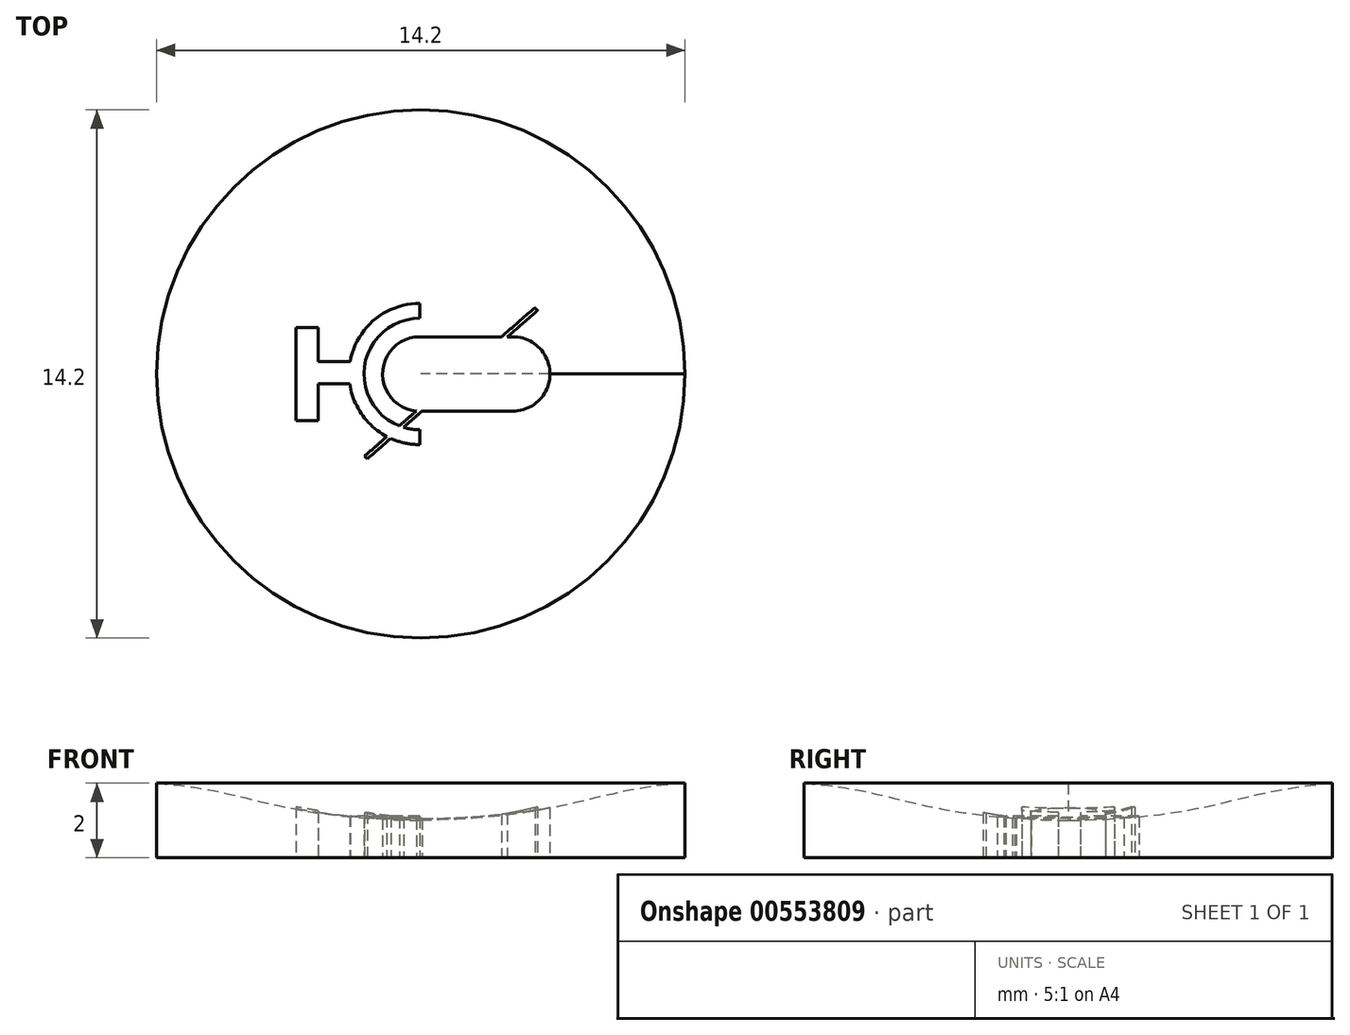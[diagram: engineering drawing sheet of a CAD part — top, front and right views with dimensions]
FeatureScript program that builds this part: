
annotation { "Feature Type Name" : "Feature", "Feature Type Description" : "" }
export const myFeature = defineFeature(function(context is Context, id is Id, definition is map)
    precondition{}
    {
        {
            var Q0;
            Q0=qCreatedBy(makeId("Front.planeOp"),FACE);
            var sketch = newSketch(context, id + "F0", { "sketchPlane" : qUnion([Q0])});
            skLineSegment(sketch, "E0", {"start": v(0, 0) * mm, "end": v(7.1, 0) * mm});
            skLineSegment(sketch, "E1", {"start": v(7.1, 0) * mm, "end": v(7.1, 2) * mm});
            skLineSegment(sketch, "E2", {"start": v(0, 1) * mm, "end": v(0, 0) * mm});
            skFitSpline(sketch, "E3", {"points": [v(7.1, 2) * mm, v(0, 1) * mm], "startDerivative": vector(-7.89, -0.57) * mm, "endDerivative": vector(-12, -0.18) * mm});
            skPoint(sketch, "E4.orphan", {"position": v(0, 2) * mm});
            skSolve(sketch);
        }
        {
            var Q0;
            Q0=makeQuery(id+"F0.imprint","IMPRINT",FACE,{"disambiguationData":[TD([[makeQuery(id+"F0.imprint","IMPRINT",EDGE,{"derivedFrom":sQuery(id+"F0.wireOp",EDGE,"E0")}),1.0]])]});
            var Q1;
            Q1=sQuery(id+"F0.wireOp",EDGE,"E2");
            revolve(context, id + "F1", {"entities" : qUnion([Q0]), "axis" : qUnion([Q1]), "revolveType" : RevolveType.FULL});
        }
        {
            var Q0;
            Q0=makeQuery(id+"F1.opRevolve","SWEPT_FACE",FACE,{"disambiguationData":[OSD([sQuery(id+"F0.wireOp",EDGE,"E0")])]});
            var sketch = newSketch(context, id + "F2", { "sketchPlane" : qUnion([Q0])});
            skLineSegment(sketch, "E5.bottom", {"start": v(2.47, 1) * mm, "end": v(0.04, 1) * mm});
            skLineSegment(sketch, "E5.top", {"start": v(2.47, -1) * mm, "end": v(2.33, -1) * mm});
            skArc(sketch, "E6", {"start": v(-0.12, 1) * mm, "mid": v(-1.03, -0.05) * mm, "end": v(-0.03, -1) * mm});
            skArc(sketch, "E7", {"start": v(2.47, -1) * mm, "mid": v(3.47, 0) * mm, "end": v(2.47, 1) * mm});
            skArc(sketch, "E8", {"start": v(-0.03, 1.5) * mm, "mid": v(-0.25, 1.48) * mm, "end": v(-0.46, 1.44) * mm});
            skArc(sketch, "E9.0", {"start": v(-0.03, 1.9) * mm, "mid": v(-0.42, 1.86) * mm, "end": v(-0.8, 1.73) * mm});
            skLineSegment(sketch, "E10", {"start": v(-0.03, -1.9) * mm, "end": v(-0.03, -1.5) * mm});
            skLineSegment(sketch, "E11.trimOffspring", {"start": v(-0.03, 1.5) * mm, "end": v(-0.03, 1.9) * mm});
            skLineSegment(sketch, "E12.bottom", {"start": v(-1.9, 0.27) * mm, "end": v(-2.75, 0.27) * mm});
            skLineSegment(sketch, "E12.top", {"start": v(-1.9, -0.33) * mm, "end": v(-2.75, -0.33) * mm});
            skLineSegment(sketch, "E13.bottom", {"start": v(-3.35, 1.25) * mm, "end": v(-2.75, 1.25) * mm});
            skLineSegment(sketch, "E13.top", {"start": v(-3.35, -1.25) * mm, "end": v(-2.75, -1.25) * mm});
            skLineSegment(sketch, "E13.left", {"start": v(-3.35, 1.25) * mm, "end": v(-3.35, -1.25) * mm});
            skLineSegment(sketch, "E13.right", {"start": v(-2.75, 1.25) * mm, "end": v(-2.75, 0.27) * mm});
            skLineSegment(sketch, "E14.trimOffspring", {"start": v(-2.75, -0.33) * mm, "end": v(-2.75, -1.25) * mm});
            skArc(sketch, "E15.trimOffspring", {"start": v(-1.9, -0.33) * mm, "mid": v(-1.25, -1.46) * mm, "end": v(-0.03, -1.9) * mm});
            skLineSegment(sketch, "E16", {"start": v(-1.95, -0.33) * mm, "end": v(-1.9, -0.33) * mm});
            skLineSegment(sketch, "E17", {"start": v(-1.43, 2.28) * mm, "end": v(-0.8, 1.73) * mm});
            skLineSegment(sketch, "E18", {"start": v(3.14, -1.7) * mm, "end": v(3.07, -1.78) * mm});
            skLineSegment(sketch, "E19", {"start": v(3.07, -1.78) * mm, "end": v(2.17, -1) * mm});
            skLineSegment(sketch, "E20", {"start": v(-1.5, 2.2) * mm, "end": v(-1.43, 2.28) * mm});
            skLineSegment(sketch, "E21.trimOffspring", {"start": v(-0.12, 1) * mm, "end": v(-0.58, 1.4) * mm});
            skLineSegment(sketch, "E22.trimOffspring", {"start": v(2.33, -1) * mm, "end": v(3.14, -1.7) * mm});
            skLineSegment(sketch, "E23.trimOffspring", {"start": v(-0.46, 1.44) * mm, "end": v(0.04, 1) * mm});
            skLineSegment(sketch, "E24.trimOffspring", {"start": v(-0.9, 1.68) * mm, "end": v(-1.5, 2.2) * mm});
            skArc(sketch, "E25.trimOffspring", {"start": v(-0.58, 1.4) * mm, "mid": v(-1.5, -0.28) * mm, "end": v(-0.03, -1.5) * mm});
            skArc(sketch, "E26.trimOffspring", {"start": v(-0.9, 1.68) * mm, "mid": v(-1.58, 1.1) * mm, "end": v(-1.9, 0.27) * mm});
            skLineSegment(sketch, "E27.trimOffspring", {"start": v(2.17, -1) * mm, "end": v(-0.03, -1) * mm});
            skSolve(sketch);
        }
        {
            var Q0;
            Q0=makeQuery(id+"F2.imprint","IMPRINT",FACE,{"disambiguationData":[TD([[makeQuery(id+"F2.imprint","IMPRINT",EDGE,{"derivedFrom":sQuery(id+"F2.wireOp",EDGE,"E5.bottom")}),1.0]])]});
            extrude(context, id + "F3", {"entities" : qUnion([Q0]), "endBound" : BoundingType.UP_TO_NEXT, "oppositeDirection" : true, "depth" : 25 * mm, "hasOffset" : true, "offsetDistance" : 0.02 * mm, "offsetOppositeDirection" : true});
        }
    });
